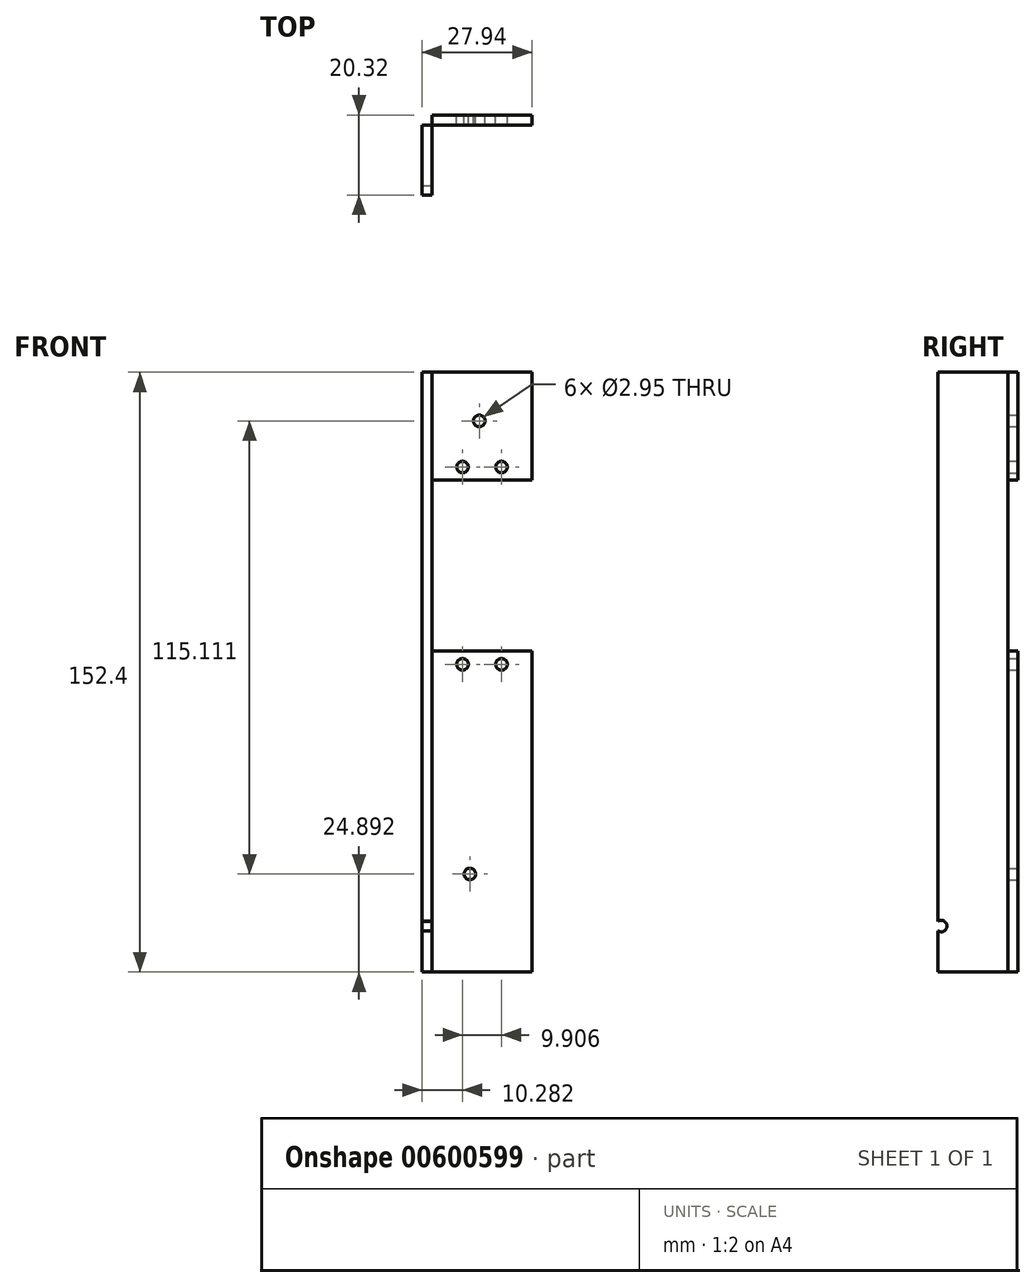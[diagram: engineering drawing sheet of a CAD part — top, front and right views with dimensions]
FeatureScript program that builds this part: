
annotation { "Feature Type Name" : "Feature", "Feature Type Description" : "" }
export const myFeature = defineFeature(function(context is Context, id is Id, definition is map)
    precondition{}
    {
        {
            var Q0;
            Q0=qCreatedBy(makeId("Top.planeOp"),FACE);
            var sketch = newSketch(context, id + "F0", { "sketchPlane" : qUnion([Q0])});
            skLineSegment(sketch, "E0.bottom", {"start": v(-10.6, -5.83) * mm, "end": v(-8.06, -5.83) * mm});
            skLineSegment(sketch, "E0.top", {"start": v(-10.6, -26.15) * mm, "end": v(-8.06, -26.15) * mm});
            skLineSegment(sketch, "E0.left", {"start": v(-10.6, -5.83) * mm, "end": v(-10.6, -26.15) * mm});
            skLineSegment(sketch, "E0.right", {"start": v(-8.06, -5.83) * mm, "end": v(-8.06, -26.15) * mm});
            skLineSegment(sketch, "E1.bottom", {"start": v(-10.6, -5.83) * mm, "end": v(17.34, -5.83) * mm});
            skLineSegment(sketch, "E1.top", {"start": v(-10.6, -8.37) * mm, "end": v(17.34, -8.37) * mm});
            skLineSegment(sketch, "E1.left", {"start": v(-10.6, -5.83) * mm, "end": v(-10.6, -8.37) * mm});
            skLineSegment(sketch, "E1.right", {"start": v(17.34, -5.83) * mm, "end": v(17.34, -8.37) * mm});
            skSolve(sketch);
        }
        {
            var Q0;
            {var subQ0=sQuery(id+"F0.wireOp",EDGE,"E0.top");Q0=makeQuery(id+"F0.imprint","IMPRINT",FACE,{"disambiguationData":[TD([[makeQuery(id+"F0.imprint","IMPRINT",EDGE,{"derivedFrom":subQ0}),1.0]])]});}
            var Q1;
            {var subQ5=sQuery(id+"F0.wireOp",EDGE,"E1.left");Q1=makeQuery(id+"F0.imprint","IMPRINT",FACE,{"disambiguationData":[TD([[makeQuery(id+"F0.imprint","IMPRINT",EDGE,{"derivedFrom":subQ5}),1.0]])]});}
            var Q2;
            {var subQ5=sQuery(id+"F0.wireOp",EDGE,"E1.right");Q2=makeQuery(id+"F0.imprint","IMPRINT",FACE,{"disambiguationData":[TD([[makeQuery(id+"F0.imprint","IMPRINT",EDGE,{"derivedFrom":subQ5}),-1.0]])]});}
            var Q3;
            Q3 = qSketchRegion(id + "F2", true);
            extrude(context, id + "F1", {"entities" : qUnion([Q0, Q1, Q2, Q3]), "depth" : 152.4 * mm, "offsetDistance" : 25.4 * mm});
        }
        {
            var Q0;
            Q0=makeQuery(id+"F1.opExtrude","SWEPT_FACE",FACE,{"disambiguationData":[OSD([sQuery(id+"F0.wireOp",EDGE,"E1.bottom")])]});
            var sketch = newSketch(context, id + "F2", { "sketchPlane" : qUnion([Q0])});
            skCircle(sketch, "E2.MirrorC", {"center": v(0.32, 78.17) * mm, "radius": 1.1 * mm});
            skLineSegment(sketch, "E3.bottom", {"start": v(8.06, 124.95) * mm, "end": v(-17.34, 124.95) * mm});
            skLineSegment(sketch, "E3.top", {"start": v(8.06, 81.51) * mm, "end": v(-17.34, 81.51) * mm});
            skLineSegment(sketch, "E3.left", {"start": v(8.06, 124.95) * mm, "end": v(8.06, 81.51) * mm});
            skLineSegment(sketch, "E3.right", {"start": v(-17.34, 124.95) * mm, "end": v(-17.34, 81.51) * mm});
            skLineSegment(sketch, "E4", {"start": v(8.06, 103.23) * mm, "end": v(-17.34, 103.23) * mm});
            skLineSegment(sketch, "E5", {"start": v(-4.64, 124.95) * mm, "end": v(-4.64, 81.51) * mm});
            skCircle(sketch, "E6.MirrorC", {"center": v(-9.59, 78.17) * mm, "radius": 1.1 * mm});
            skLineSegment(sketch, "E7.MirrorCS", {"start": v(-17.34, 103.23) * mm, "end": v(8.06, 103.23) * mm});
            skCircle(sketch, "E8.MirrorC", {"center": v(0.32, 128.3) * mm, "radius": 1.1 * mm});
            skCircle(sketch, "E9.MirrorC", {"center": v(-9.59, 128.3) * mm, "radius": 1.1 * mm});
            skCircle(sketch, "E10", {"center": v(-3.94, 140) * mm, "radius": 3.69 * mm});
            skCircle(sketch, "E11", {"center": v(-1.56, 24.9) * mm, "radius": 4.27 * mm});
            skSolve(sketch);
        }
        {
            var Q0;
            Q0=makeQuery(id+"F1.opExtrude","SWEPT_FACE",FACE,{"disambiguationData":[OSD([sQuery(id+"F0.wireOp",EDGE,"E0.left"),sQuery(id+"F0.wireOp",EDGE,"E1.left")])]});
            var sketch = newSketch(context, id + "F3", { "sketchPlane" : qUnion([Q0])});
            skCircle(sketch, "E12", {"center": v(25.3, 11.67) * mm, "radius": 2.53 * mm});
            skSolve(sketch);
        }
        {
            var Q0;
            Q0=sQuery(id+"F2.wireOp",VERTEX,"E2.MirrorC.center");
            var Q1;
            Q1=makeQuery(id+"F1.opExtrude","SWEPT_BODY",BODY,{"disambiguationData":[OSD([sQuery(id+"F0.wireOp",EDGE,"E0.top"),sQuery(id+"F0.wireOp",EDGE,"E0.left"),sQuery(id+"F0.wireOp",EDGE,"E0.right"),sQuery(id+"F0.wireOp",EDGE,"E1.bottom"),sQuery(id+"F0.wireOp",EDGE,"E1.top"),sQuery(id+"F0.wireOp",EDGE,"E1.left"),sQuery(id+"F0.wireOp",EDGE,"E1.right")])]});
            hole(context, id + "F4", {"style" : HoleStyle.SIMPLE, "endStyle" : HoleEndStyle.THROUGH, "holeDiameter" : 2.95 * mm, "majorDiameter" : 6.35 * mm, "isTappedThrough" : true, "tappedDepth" : 12.7 * mm, "tapClearance" : 3, "locations" : qUnion([Q0]), "scope" : qUnion([Q1])});
        }
        {
            var Q0;
            {var subQ0=sQuery(id+"F2.wireOp",EDGE,"E3.left");var subQ1=sQuery(id+"F2.wireOp",EDGE,"E3.bottom");var subQ2=makeQuery(id+"F2.imprint","INTERSECT",VERTEX,{"derivedFrom":[subQ1,subQ0]});Q0=makeQuery(id+"F2.imprint","IMPRINT",FACE,{"disambiguationData":[TD([[makeQuery(id+"F2.imprint","IMPRINT",EDGE,{"disambiguationData":[TD([[subQ2,-1.0]])],"derivedFrom":subQ1}),1.0]])]});}
            var Q1;
            {var subQ0=sQuery(id+"F2.wireOp",EDGE,"E3.left");var subQ1=sQuery(id+"F2.wireOp",EDGE,"E3.top");var subQ2=makeQuery(id+"F2.imprint","INTERSECT",VERTEX,{"derivedFrom":[subQ1,subQ0]});Q1=makeQuery(id+"F2.imprint","IMPRINT",FACE,{"disambiguationData":[TD([[makeQuery(id+"F2.imprint","IMPRINT",EDGE,{"disambiguationData":[TD([[subQ2,-1.0]])],"derivedFrom":subQ1}),-1.0]])]});}
            var Q2;
            {var subQ1=sQuery(id+"F2.wireOp",EDGE,"E3.bottom");var subQ3=sQuery(id+"F2.wireOp",EDGE,"E5");var subQ4=makeQuery(id+"F2.imprint","INTERSECT",VERTEX,{"derivedFrom":[subQ1,subQ3]});Q2=makeQuery(id+"F2.imprint","IMPRINT",FACE,{"disambiguationData":[TD([[makeQuery(id+"F2.imprint","IMPRINT",EDGE,{"disambiguationData":[TD([[subQ4,-1.0]])],"derivedFrom":subQ3}),-1.0]])]});}
            var Q3;
            {var subQ1=sQuery(id+"F2.wireOp",EDGE,"E3.top");var subQ3=sQuery(id+"F2.wireOp",EDGE,"E5");var subQ4=makeQuery(id+"F2.imprint","INTERSECT",VERTEX,{"derivedFrom":[subQ1,subQ3]});Q3=makeQuery(id+"F2.imprint","IMPRINT",FACE,{"disambiguationData":[TD([[makeQuery(id+"F2.imprint","IMPRINT",EDGE,{"disambiguationData":[TD([[subQ4,1.0]])],"derivedFrom":subQ3}),-1.0]])]});}
            extrude(context, id + "F5", {"entities" : qUnion([Q0, Q1, Q2, Q3]), "operationType" : NewBodyOperationType.REMOVE, "endBound" : BoundingType.SYMMETRIC, "oppositeDirection" : true, "depth" : 5.08 * mm, "offsetDistance" : 25.4 * mm});
        }
        {
            var Q0;
            Q0=sQuery(id+"F2.wireOp",VERTEX,"E8.MirrorC.center");
            var Q1;
            Q1=makeQuery(id+"F1.opExtrude","SWEPT_BODY",BODY,{"disambiguationData":[OSD([sQuery(id+"F0.wireOp",EDGE,"E0.top"),sQuery(id+"F0.wireOp",EDGE,"E0.left"),sQuery(id+"F0.wireOp",EDGE,"E0.right"),sQuery(id+"F0.wireOp",EDGE,"E1.bottom"),sQuery(id+"F0.wireOp",EDGE,"E1.top"),sQuery(id+"F0.wireOp",EDGE,"E1.left"),sQuery(id+"F0.wireOp",EDGE,"E1.right")])]});
            hole(context, id + "F6", {"style" : HoleStyle.SIMPLE, "endStyle" : HoleEndStyle.THROUGH, "holeDiameter" : 2.95 * mm, "majorDiameter" : 6.35 * mm, "isTappedThrough" : true, "tappedDepth" : 12.7 * mm, "tapClearance" : 3, "locations" : qUnion([Q0]), "scope" : qUnion([Q1])});
        }
        {
            var Q0;
            Q0=sQuery(id+"F2.wireOp",VERTEX,"E9.MirrorC.center");
            var Q1;
            Q1=makeQuery(id+"F1.opExtrude","SWEPT_BODY",BODY,{"disambiguationData":[OSD([sQuery(id+"F0.wireOp",EDGE,"E0.top"),sQuery(id+"F0.wireOp",EDGE,"E0.left"),sQuery(id+"F0.wireOp",EDGE,"E0.right"),sQuery(id+"F0.wireOp",EDGE,"E1.bottom"),sQuery(id+"F0.wireOp",EDGE,"E1.top"),sQuery(id+"F0.wireOp",EDGE,"E1.left"),sQuery(id+"F0.wireOp",EDGE,"E1.right")])]});
            hole(context, id + "F7", {"style" : HoleStyle.SIMPLE, "endStyle" : HoleEndStyle.THROUGH, "holeDiameter" : 2.95 * mm, "majorDiameter" : 6.35 * mm, "isTappedThrough" : true, "tappedDepth" : 12.7 * mm, "tapClearance" : 3, "locations" : qUnion([Q0]), "scope" : qUnion([Q1])});
        }
        {
            var Q0;
            Q0=sQuery(id+"F2.wireOp",VERTEX,"E6.MirrorC.center");
            var Q1;
            Q1=makeQuery(id+"F1.opExtrude","SWEPT_BODY",BODY,{"disambiguationData":[OSD([sQuery(id+"F0.wireOp",EDGE,"E0.top"),sQuery(id+"F0.wireOp",EDGE,"E0.left"),sQuery(id+"F0.wireOp",EDGE,"E0.right"),sQuery(id+"F0.wireOp",EDGE,"E1.bottom"),sQuery(id+"F0.wireOp",EDGE,"E1.top"),sQuery(id+"F0.wireOp",EDGE,"E1.left"),sQuery(id+"F0.wireOp",EDGE,"E1.right")])]});
            hole(context, id + "F8", {"style" : HoleStyle.SIMPLE, "endStyle" : HoleEndStyle.THROUGH, "holeDiameter" : 2.95 * mm, "majorDiameter" : 6.35 * mm, "isTappedThrough" : true, "tappedDepth" : 12.7 * mm, "tapClearance" : 3, "locations" : qUnion([Q0]), "scope" : qUnion([Q1])});
        }
        {
            var Q0;
            Q0=sQuery(id+"F2.wireOp",VERTEX,"E10.center");
            var Q1;
            Q1=makeQuery(id+"F1.opExtrude","SWEPT_BODY",BODY,{"disambiguationData":[OSD([sQuery(id+"F0.wireOp",EDGE,"E0.top"),sQuery(id+"F0.wireOp",EDGE,"E0.left"),sQuery(id+"F0.wireOp",EDGE,"E0.right"),sQuery(id+"F0.wireOp",EDGE,"E1.bottom"),sQuery(id+"F0.wireOp",EDGE,"E1.top"),sQuery(id+"F0.wireOp",EDGE,"E1.left"),sQuery(id+"F0.wireOp",EDGE,"E1.right")])]});
            hole(context, id + "F9", {"style" : HoleStyle.SIMPLE, "endStyle" : HoleEndStyle.THROUGH, "holeDiameter" : 2.95 * mm, "majorDiameter" : 6.35 * mm, "isTappedThrough" : true, "tappedDepth" : 12.7 * mm, "tapClearance" : 3, "locations" : qUnion([Q0]), "scope" : qUnion([Q1])});
        }
        {
            var Q0;
            Q0=sQuery(id+"F2.wireOp",VERTEX,"E11.center");
            var Q1;
            Q1=makeQuery(id+"F1.opExtrude","SWEPT_BODY",BODY,{"disambiguationData":[OSD([sQuery(id+"F0.wireOp",EDGE,"E0.top"),sQuery(id+"F0.wireOp",EDGE,"E0.left"),sQuery(id+"F0.wireOp",EDGE,"E0.right"),sQuery(id+"F0.wireOp",EDGE,"E1.bottom"),sQuery(id+"F0.wireOp",EDGE,"E1.top"),sQuery(id+"F0.wireOp",EDGE,"E1.left"),sQuery(id+"F0.wireOp",EDGE,"E1.right")])]});
            hole(context, id + "F10", {"style" : HoleStyle.SIMPLE, "endStyle" : HoleEndStyle.THROUGH, "holeDiameter" : 2.95 * mm, "majorDiameter" : 6.35 * mm, "isTappedThrough" : true, "tappedDepth" : 12.7 * mm, "tapClearance" : 3, "locations" : qUnion([Q0]), "scope" : qUnion([Q1])});
        }
        {
            var Q0;
            Q0=sQuery(id+"F3.wireOp",VERTEX,"E12.center");
            var Q1;
            Q1=makeQuery(id+"F1.opExtrude","SWEPT_BODY",BODY,{"disambiguationData":[OSD([sQuery(id+"F0.wireOp",EDGE,"E0.top"),sQuery(id+"F0.wireOp",EDGE,"E0.left"),sQuery(id+"F0.wireOp",EDGE,"E0.right"),sQuery(id+"F0.wireOp",EDGE,"E1.bottom"),sQuery(id+"F0.wireOp",EDGE,"E1.top"),sQuery(id+"F0.wireOp",EDGE,"E1.left"),sQuery(id+"F0.wireOp",EDGE,"E1.right")])]});
            hole(context, id + "F11", {"style" : HoleStyle.SIMPLE, "endStyle" : HoleEndStyle.THROUGH, "holeDiameter" : 2.95 * mm, "majorDiameter" : 6.35 * mm, "isTappedThrough" : true, "tappedDepth" : 12.7 * mm, "tapClearance" : 3, "locations" : qUnion([Q0]), "scope" : qUnion([Q1])});
        }
    });
